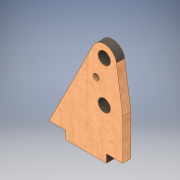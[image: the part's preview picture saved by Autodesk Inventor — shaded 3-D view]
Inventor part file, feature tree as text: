
AUTODESK INVENTOR PART (.ipt)
format: ipt  version: 2019 (Build 230136000, 136)  size: 140,800 bytes
history: native  units: mm
features: extrude x2, sketch x2, other x1
ambient origin geometry x8: Origin, YZ Plane, XZ Plane, XY Plane, X Axis, Y Axis, Z Axis, Center Point
bodies: Body1 (feature_tree)
feature tree (5):
  other  "Твердое тело1"
  extrude  "Выдавливание1"  Depth=6.0mm
  extrude  "Выдавливание2"  Depth=40.0mm
  sketch  "Эскиз1"
  sketch  "Эскиз2"
